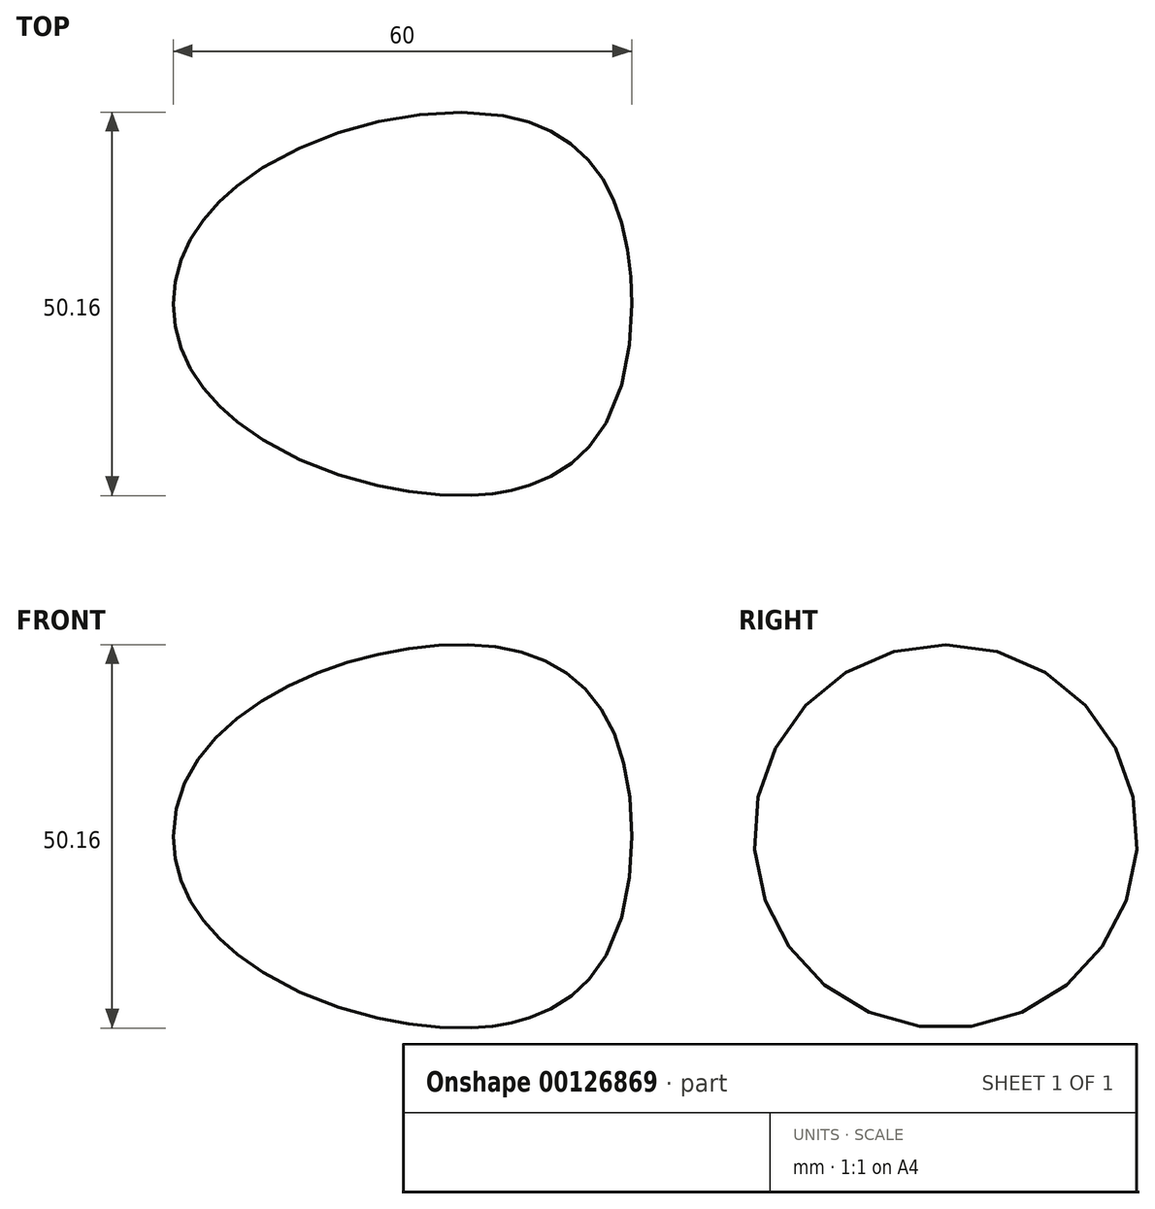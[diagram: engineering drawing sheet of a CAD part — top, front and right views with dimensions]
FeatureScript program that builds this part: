
annotation { "Feature Type Name" : "Feature", "Feature Type Description" : "" }
export const myFeature = defineFeature(function(context is Context, id is Id, definition is map)
    precondition{}
    {
        {
            var Q0;
            Q0=qCreatedBy(makeId("Front.planeOp"),FACE);
            var sketch = newSketch(context, id + "F0", { "sketchPlane" : qUnion([Q0])});
            skLineSegment(sketch, "E0", {"start": v(0, 0) * mm, "end": v(-60, 0) * mm});
            skPoint(sketch, "E1", {"position": v(-25, 0) * mm});
            skLineSegment(sketch, "E2", {"start": v(-25, 0) * mm, "end": v(-25, 25) * mm, "construction": true});
            skFitSpline(sketch, "E3", {"points": [v(-60, 0) * mm, v(-25, 25) * mm, v(0, 0) * mm], "startDerivative": vector(0, 85.8) * mm, "endDerivative": vector(0, -126.18) * mm});
            skLineSegment(sketch, "E4", {"start": v(-60, 0) * mm, "end": v(-60, 15) * mm, "construction": true});
            skLineSegment(sketch, "E5", {"start": v(-79.17, 0) * mm, "end": v(0, 45.7) * mm, "construction": true});
            skLineSegment(sketch, "E6", {"start": v(0, 0) * mm, "end": v(-79.17, 0) * mm, "construction": true});
            skPoint(sketch, "E7", {"position": v(-47.13, 18.5) * mm});
            skLineSegment(sketch, "E8", {"start": v(-47.13, 18.5) * mm, "end": v(-61.96, 44.2) * mm, "construction": true});
            skLineSegment(sketch, "E9", {"start": v(0, 0) * mm, "end": v(0, 56.9) * mm, "construction": true});
            skSolve(sketch);
        }
        {
            var Q0;
            Q0 = qSketchRegion(id + "F0", true);
            var Q1;
            Q1 = qConstructionFilter(qBodyType(qCreatedBy(id + "F0" ,EDGE), BodyType.WIRE), ConstructionObject.NO);
            var Q2;
            Q2=sQuery(id+"F0.wireOp",EDGE,"E0");
            revolve(context, id + "F1", {"entities" : qUnion([Q0]), "surfaceEntities" : qUnion([Q1]), "axis" : qUnion([Q2]), "revolveType" : RevolveType.FULL});
        }
    });
